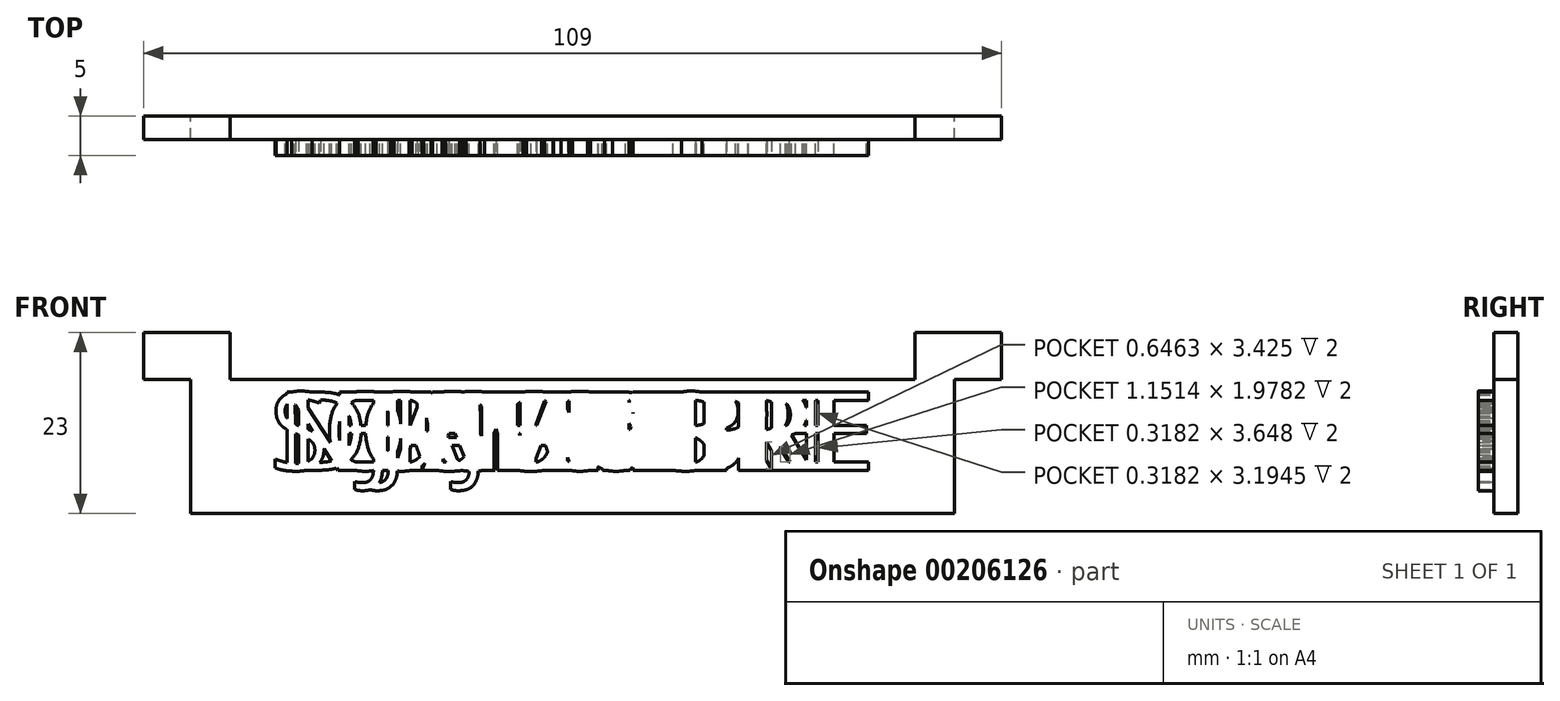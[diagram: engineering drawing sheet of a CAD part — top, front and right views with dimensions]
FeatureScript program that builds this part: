
annotation { "Feature Type Name" : "Feature", "Feature Type Description" : "" }
export const myFeature = defineFeature(function(context is Context, id is Id, definition is map)
    precondition{}
    {
        {
            var Q0;
            Q0=qCreatedBy(makeId("Front.planeOp"),FACE);
            var sketch = newSketch(context, id + "F0", { "sketchPlane" : qUnion([Q0])});
            skLineSegment(sketch, "E0.bottom", {"start": v(-51.5, 23) * mm, "end": v(-40.5, 23) * mm});
            skLineSegment(sketch, "E0.top", {"start": v(-45.5, 0) * mm, "end": v(51.5, 0) * mm});
            skLineSegment(sketch, "E0.left", {"start": v(-51.5, 23) * mm, "end": v(-51.5, 17) * mm});
            skLineSegment(sketch, "E0.right", {"start": v(57.5, 23) * mm, "end": v(57.5, 17) * mm});
            skLineSegment(sketch, "E1.top", {"start": v(-51.5, 17) * mm, "end": v(-45.5, 17) * mm});
            skLineSegment(sketch, "E1.right", {"start": v(-45.5, 0) * mm, "end": v(-45.5, 17) * mm});
            skLineSegment(sketch, "E2.bottom", {"start": v(-51.5, 23) * mm, "end": v(-40.5, 23) * mm, "construction": true});
            skLineSegment(sketch, "E2.top", {"start": v(-51.5, 17) * mm, "end": v(-40.5, 17) * mm, "construction": true});
            skLineSegment(sketch, "E2.left", {"start": v(-51.5, 23) * mm, "end": v(-51.5, 17) * mm, "construction": true});
            skLineSegment(sketch, "E2.right", {"start": v(-40.5, 23) * mm, "end": v(-40.5, 17) * mm, "construction": true});
            skLineSegment(sketch, "E3.top", {"start": v(-40.5, 17) * mm, "end": v(46.5, 17) * mm});
            skLineSegment(sketch, "E3.left", {"start": v(-40.5, 23) * mm, "end": v(-40.5, 17) * mm});
            skLineSegment(sketch, "E3.right", {"start": v(46.5, 23) * mm, "end": v(46.5, 17) * mm});
            skLineSegment(sketch, "E4.top", {"start": v(57.5, 17) * mm, "end": v(51.5, 17) * mm});
            skLineSegment(sketch, "E4.right", {"start": v(51.5, 0) * mm, "end": v(51.5, 17) * mm});
            skLineSegment(sketch, "E5.trimOffspring", {"start": v(46.5, 23) * mm, "end": v(57.5, 23) * mm});
            skSolve(sketch);
        }
        {
            var Q0;
            Q0=makeQuery(id+"F0.imprint","IMPRINT",FACE,{"disambiguationData":[TD([[makeQuery(id+"F0.imprint","IMPRINT",EDGE,{"derivedFrom":sQuery(id+"F0.wireOp",EDGE,"E0.bottom")}),-1.0]])]});
            extrude(context, id + "F1", {"entities" : qUnion([Q0]), "depth" : 3 * mm});
        }
        {
            var Q0;
            Q0=makeQuery(id+"F1.opExtrude","CAP_FACE",FACE,{"disambiguationData":[OSD([sQuery(id+"F0.wireOp",EDGE,"E0.bottom"),sQuery(id+"F0.wireOp",EDGE,"E0.top"),sQuery(id+"F0.wireOp",EDGE,"E0.left"),sQuery(id+"F0.wireOp",EDGE,"E0.right"),sQuery(id+"F0.wireOp",EDGE,"E1.top"),sQuery(id+"F0.wireOp",EDGE,"E1.right"),sQuery(id+"F0.wireOp",EDGE,"E3.top"),sQuery(id+"F0.wireOp",EDGE,"E3.left"),sQuery(id+"F0.wireOp",EDGE,"E3.right"),sQuery(id+"F0.wireOp",EDGE,"E4.top"),sQuery(id+"F0.wireOp",EDGE,"E4.right"),sQuery(id+"F0.wireOp",EDGE,"E5.trimOffspring")])],"isStart":false});
            var sketch = newSketch(context, id + "F2", { "sketchPlane" : qUnion([Q0])});
            skLineSegment(sketch, "E6.0", {"start": v(-45.5, 3.5) * mm, "end": v(-42, 3.5) * mm, "construction": true});
            skLineSegment(sketch, "E7.0", {"start": v(-42, 15.5) * mm, "end": v(48, 15.5) * mm, "construction": true});
            skLineSegment(sketch, "E8.0", {"start": v(-42, 0) * mm, "end": v(-42, 15.5) * mm, "construction": true});
            skText(sketch, "E9", { "text": "JANVIER", "fontName": "OpenSans-Regular.ttf"});
            skLineSegment(sketch, "E10.top", {"start": v(-45.5, 0) * mm, "end": v(-42, 0) * mm, "construction": true});
            skLineSegment(sketch, "E10.left", {"start": v(-45.5, 3.5) * mm, "end": v(-45.5, 0) * mm, "construction": true});
            skLineSegment(sketch, "E10.right", {"start": v(-42, 3.5) * mm, "end": v(-42, 0) * mm, "construction": true});
            skLineSegment(sketch, "E11.0", {"start": v(48, 0) * mm, "end": v(48, 17) * mm, "construction": true});
            skPoint(sketch, "E12.orphan", {"position": v(48, 15.5) * mm});
            skPoint(sketch, "E13.end.orphan", {"position": v(3, 0) * mm});
            skLineSegment(sketch, "E14", {"start": v(3, 17) * mm, "end": v(3, 0) * mm, "construction": true});
            const initialGuessF2  = {"E9": [-0.02358, 0.0055, 1, 0, 0.01]};
            skSetInitialGuess(sketch, initialGuessF2);
            skSolve(sketch);
        }
        {
            var Q0;
            Q0=makeQuery(id+"F2.imprint","IMPRINT",FACE,{"disambiguationData":[TD([[makeQuery(id+"F2.imprint","IMPRINT",EDGE,{"derivedFrom":sQuery(id+"F2.wireOp",EDGE,"E9.sketch_text.stroke-0")}),-1.0]])]});
            var Q1;
            Q1=makeQuery(id+"F2.imprint","IMPRINT",FACE,{"disambiguationData":[TD([[makeQuery(id+"F2.imprint","IMPRINT",EDGE,{"derivedFrom":sQuery(id+"F2.wireOp",EDGE,"E9.sketch_text.stroke-10")}),-1.0]])]});
            var Q2;
            Q2=makeQuery(id+"F2.imprint","IMPRINT",FACE,{"disambiguationData":[TD([[makeQuery(id+"F2.imprint","IMPRINT",EDGE,{"derivedFrom":sQuery(id+"F2.wireOp",EDGE,"E9.sketch_text.stroke-23")}),-1.0]])]});
            var Q3;
            Q3=makeQuery(id+"F2.imprint","IMPRINT",FACE,{"disambiguationData":[TD([[makeQuery(id+"F2.imprint","IMPRINT",EDGE,{"derivedFrom":sQuery(id+"F2.wireOp",EDGE,"E9.sketch_text.stroke-38")}),-1.0]])]});
            var Q4;
            Q4=makeQuery(id+"F2.imprint","IMPRINT",FACE,{"disambiguationData":[TD([[makeQuery(id+"F2.imprint","IMPRINT",EDGE,{"derivedFrom":sQuery(id+"F2.wireOp",EDGE,"E9.sketch_text.stroke-52")}),-1.0]])]});
            var Q5;
            Q5=makeQuery(id+"F2.imprint","IMPRINT",FACE,{"disambiguationData":[TD([[makeQuery(id+"F2.imprint","IMPRINT",EDGE,{"derivedFrom":sQuery(id+"F2.wireOp",EDGE,"E9.sketch_text.stroke-65")}),-1.0]])]});
            var Q6;
            Q6=makeQuery(id+"F2.imprint","IMPRINT",FACE,{"disambiguationData":[TD([[makeQuery(id+"F2.imprint","IMPRINT",EDGE,{"derivedFrom":sQuery(id+"F2.wireOp",EDGE,"E9.sketch_text.stroke-47")}),-1.0]])]});
            extrude(context, id + "F3", {"entities" : qUnion([Q0, Q1, Q2, Q3, Q4, Q5, Q6]), "operationType" : NewBodyOperationType.ADD, "depth" : 2 * mm});
        }
        {
            var Q0;
            Q0=qSketchRegion(id+"F0",true);
            extrude(context, id + "F4", {"entities" : qUnion([Q0]), "depth" : 3 * mm});
        }
        {
            var Q0;
            Q0=makeQuery(id+"F4.opExtrude","CAP_FACE",FACE,{"disambiguationData":[OSD([sQuery(id+"F0.wireOp",EDGE,"E0.bottom"),sQuery(id+"F0.wireOp",EDGE,"E0.top"),sQuery(id+"F0.wireOp",EDGE,"E0.left"),sQuery(id+"F0.wireOp",EDGE,"E0.right"),sQuery(id+"F0.wireOp",EDGE,"E1.top"),sQuery(id+"F0.wireOp",EDGE,"E1.right"),sQuery(id+"F0.wireOp",EDGE,"E3.top"),sQuery(id+"F0.wireOp",EDGE,"E3.left"),sQuery(id+"F0.wireOp",EDGE,"E3.right"),sQuery(id+"F0.wireOp",EDGE,"E4.top"),sQuery(id+"F0.wireOp",EDGE,"E4.right"),sQuery(id+"F0.wireOp",EDGE,"E5.trimOffspring")])],"isStart":false});
            var sketch = newSketch(context, id + "F5", { "sketchPlane" : qUnion([Q0])});
            skText(sketch, "E15", { "text": "FEVRIER", "fontName": "OpenSans-Regular.ttf"});
            skPoint(sketch, "E16.orphan", {"position": v(40.68, 15.5) * mm});
            skPoint(sketch, "E17.end.orphan", {"position": v(-0.5, 0) * mm});
            skPoint(sketch, "E18.orphan", {"position": v(-34.68, 15.5) * mm});
            skLineSegment(sketch, "E19.0", {"start": v(-43.5, 15.5) * mm, "end": v(49.5, 15.5) * mm, "construction": true});
            skPoint(sketch, "E20.start.orphan", {"position": v(3, 17) * mm});
            const initialGuessF5  = {"E15": [-0.0233, 0.0055, 1, 0, 0.01]};
            skSetInitialGuess(sketch, initialGuessF5);
            skSolve(sketch);
        }
        {
            var Q0;
            Q0=makeQuery(id+"F5.imprint","IMPRINT",FACE,{"disambiguationData":[TD([[makeQuery(id+"F5.imprint","IMPRINT",EDGE,{"derivedFrom":sQuery(id+"F5.wireOp",EDGE,"E15.sketch_text.stroke-0")}),-1.0]])]});
            var Q1;
            Q1=makeQuery(id+"F5.imprint","IMPRINT",FACE,{"disambiguationData":[TD([[makeQuery(id+"F5.imprint","IMPRINT",EDGE,{"derivedFrom":sQuery(id+"F5.wireOp",EDGE,"E15.sketch_text.stroke-10")}),-1.0]])]});
            var Q2;
            Q2=makeQuery(id+"F5.imprint","IMPRINT",FACE,{"disambiguationData":[TD([[makeQuery(id+"F5.imprint","IMPRINT",EDGE,{"derivedFrom":sQuery(id+"F5.wireOp",EDGE,"E15.sketch_text.stroke-22")}),-1.0]])]});
            var Q3;
            Q3=makeQuery(id+"F5.imprint","IMPRINT",FACE,{"disambiguationData":[TD([[makeQuery(id+"F5.imprint","IMPRINT",EDGE,{"derivedFrom":sQuery(id+"F5.wireOp",EDGE,"E15.sketch_text.stroke-47")}),-1.0]])]});
            var Q4;
            Q4=makeQuery(id+"F5.imprint","IMPRINT",FACE,{"disambiguationData":[TD([[makeQuery(id+"F5.imprint","IMPRINT",EDGE,{"derivedFrom":sQuery(id+"F5.wireOp",EDGE,"E15.sketch_text.stroke-65")}),-1.0]])]});
            var Q5;
            Q5=makeQuery(id+"F5.imprint","IMPRINT",FACE,{"disambiguationData":[TD([[makeQuery(id+"F5.imprint","IMPRINT",EDGE,{"derivedFrom":sQuery(id+"F5.wireOp",EDGE,"E15.sketch_text.stroke-79")}),-1.0]])]});
            var Q6;
            Q6=makeQuery(id+"F2.imprint","IMPRINT",FACE,{"disambiguationData":[TD([[makeQuery(id+"F2.imprint","IMPRINT",EDGE,{"derivedFrom":sQuery(id+"F2.wireOp",EDGE,"E9.sketch_text.stroke-51")}),-1.0]])]});
            var Q7;
            Q7=makeQuery(id+"F2.imprint","IMPRINT",FACE,{"disambiguationData":[TD([[makeQuery(id+"F2.imprint","IMPRINT",EDGE,{"derivedFrom":sQuery(id+"F2.wireOp",EDGE,"E9.sketch_text.stroke-47")}),-1.0]])]});
            extrude(context, id + "F6", {"entities" : qUnion([Q0, Q1, Q2, Q3, Q4, Q5, Q6, Q7]), "operationType" : NewBodyOperationType.ADD, "depth" : 2 * mm});
        }
        {
            var Q0;
            Q0=makeQuery(id+"F0.imprint","IMPRINT",FACE,{"disambiguationData":[TD([[makeQuery(id+"F0.imprint","IMPRINT",EDGE,{"derivedFrom":sQuery(id+"F0.wireOp",EDGE,"E0.bottom")}),-1.0]])]});
            extrude(context, id + "F7", {"entities" : qUnion([Q0]), "depth" : 3 * mm});
        }
        {
            var Q0;
            Q0=makeQuery(id+"F7.opExtrude","CAP_FACE",FACE,{"disambiguationData":[OSD([sQuery(id+"F0.wireOp",EDGE,"E0.bottom"),sQuery(id+"F0.wireOp",EDGE,"E0.top"),sQuery(id+"F0.wireOp",EDGE,"E0.left"),sQuery(id+"F0.wireOp",EDGE,"E0.right"),sQuery(id+"F0.wireOp",EDGE,"E1.top"),sQuery(id+"F0.wireOp",EDGE,"E1.right"),sQuery(id+"F0.wireOp",EDGE,"E3.top"),sQuery(id+"F0.wireOp",EDGE,"E3.left"),sQuery(id+"F0.wireOp",EDGE,"E3.right"),sQuery(id+"F0.wireOp",EDGE,"E4.top"),sQuery(id+"F0.wireOp",EDGE,"E4.right"),sQuery(id+"F0.wireOp",EDGE,"E5.trimOffspring")])],"isStart":false});
            var sketch = newSketch(context, id + "F8", { "sketchPlane" : qUnion([Q0])});
            skText(sketch, "E21", { "text": "MARS", "fontName": "OpenSans-Regular.ttf"});
            skPoint(sketch, "E22.orphan", {"position": v(33.28, 15.5) * mm});
            skPoint(sketch, "E23.end.orphan", {"position": v(0, -12.7) * mm});
            skPoint(sketch, "E24.orphan", {"position": v(-27.28, 15.5) * mm});
            skPoint(sketch, "E25.start.orphan", {"position": v(0, 4.3) * mm});
            skLineSegment(sketch, "E26.0", {"start": v(-43.5, 15.5) * mm, "end": v(49.5, 15.5) * mm, "construction": true});
            const initialGuessF8  = {"E21": [-0.01589, 0.0055, 1, 0, 0.01]};
            skSetInitialGuess(sketch, initialGuessF8);
            skSolve(sketch);
        }
        {
            var Q0;
            Q0=makeQuery(id+"F8.imprint","IMPRINT",FACE,{"disambiguationData":[TD([[makeQuery(id+"F8.imprint","IMPRINT",EDGE,{"derivedFrom":sQuery(id+"F8.wireOp",EDGE,"E21.sketch_text.stroke-0")}),-1.0]])]});
            var Q1;
            Q1=makeQuery(id+"F8.imprint","IMPRINT",FACE,{"disambiguationData":[TD([[makeQuery(id+"F8.imprint","IMPRINT",EDGE,{"derivedFrom":sQuery(id+"F8.wireOp",EDGE,"E21.sketch_text.stroke-18")}),-1.0]])]});
            var Q2;
            Q2=makeQuery(id+"F8.imprint","IMPRINT",FACE,{"disambiguationData":[TD([[makeQuery(id+"F8.imprint","IMPRINT",EDGE,{"derivedFrom":sQuery(id+"F8.wireOp",EDGE,"E21.sketch_text.stroke-31")}),-1.0]])]});
            var Q3;
            Q3=makeQuery(id+"F8.imprint","IMPRINT",FACE,{"disambiguationData":[TD([[makeQuery(id+"F8.imprint","IMPRINT",EDGE,{"derivedFrom":sQuery(id+"F8.wireOp",EDGE,"E21.sketch_text.stroke-49")}),-1.0]])]});
            var Q4;
            Q4=makeQuery(id+"F8.imprint","IMPRINT",FACE,{"disambiguationData":[TD([[makeQuery(id+"F8.imprint","IMPRINT",EDGE,{"derivedFrom":sQuery(id+"F8.wireOp",EDGE,"E21.sketch_text.stroke-64")}),-1.0]])]});
            extrude(context, id + "F9", {"entities" : qUnion([Q0, Q1, Q2, Q3, Q4]), "operationType" : NewBodyOperationType.ADD, "depth" : 2 * mm});
        }
        {
            var Q0;
            Q0=makeQuery(id+"F0.imprint","IMPRINT",FACE,{"disambiguationData":[TD([[makeQuery(id+"F0.imprint","IMPRINT",EDGE,{"derivedFrom":sQuery(id+"F0.wireOp",EDGE,"E0.bottom")}),-1.0]])]});
            extrude(context, id + "F10", {"entities" : qUnion([Q0]), "depth" : 3 * mm});
        }
        {
            var Q0;
            Q0=makeQuery(id+"F10.opExtrude","CAP_FACE",FACE,{"disambiguationData":[OSD([sQuery(id+"F0.wireOp",EDGE,"E0.bottom"),sQuery(id+"F0.wireOp",EDGE,"E0.top"),sQuery(id+"F0.wireOp",EDGE,"E0.left"),sQuery(id+"F0.wireOp",EDGE,"E0.right"),sQuery(id+"F0.wireOp",EDGE,"E1.top"),sQuery(id+"F0.wireOp",EDGE,"E1.right"),sQuery(id+"F0.wireOp",EDGE,"E3.top"),sQuery(id+"F0.wireOp",EDGE,"E3.left"),sQuery(id+"F0.wireOp",EDGE,"E3.right"),sQuery(id+"F0.wireOp",EDGE,"E4.top"),sQuery(id+"F0.wireOp",EDGE,"E4.right"),sQuery(id+"F0.wireOp",EDGE,"E5.trimOffspring")])],"isStart":false});
            var sketch = newSketch(context, id + "F11", { "sketchPlane" : qUnion([Q0])});
            skText(sketch, "E27", { "text": "AVRIL", "fontName": "OpenSans-Regular.ttf"});
            skPoint(sketch, "E28.orphan", {"position": v(33.04, 15.5) * mm});
            skPoint(sketch, "E29.end.orphan", {"position": v(0.3, -20.32) * mm});
            skPoint(sketch, "E30.orphan", {"position": v(-27.04, 15.5) * mm});
            skPoint(sketch, "E31.start.orphan", {"position": v(0.3, -3.32) * mm});
            skLineSegment(sketch, "E32.0", {"start": v(-43.5, 15.5) * mm, "end": v(49.5, 15.5) * mm});
            const initialGuessF11  = {"E27": [-0.01565, 0.0055, 1, 0, 0.01]};
            skSetInitialGuess(sketch, initialGuessF11);
            skSolve(sketch);
        }
        {
            var Q0;
            Q0=makeQuery(id+"F11.imprint","IMPRINT",FACE,{"disambiguationData":[TD([[makeQuery(id+"F11.imprint","IMPRINT",EDGE,{"derivedFrom":sQuery(id+"F11.wireOp",EDGE,"E27.sketch_text.stroke-0")}),-1.0]])]});
            var Q1;
            Q1=makeQuery(id+"F11.imprint","IMPRINT",FACE,{"disambiguationData":[TD([[makeQuery(id+"F11.imprint","IMPRINT",EDGE,{"derivedFrom":sQuery(id+"F11.wireOp",EDGE,"E27.sketch_text.stroke-13")}),-1.0]])]});
            var Q2;
            Q2=makeQuery(id+"F11.imprint","IMPRINT",FACE,{"disambiguationData":[TD([[makeQuery(id+"F11.imprint","IMPRINT",EDGE,{"derivedFrom":sQuery(id+"F11.wireOp",EDGE,"E27.sketch_text.stroke-28")}),-1.0]])]});
            var Q3;
            Q3=makeQuery(id+"F11.imprint","IMPRINT",FACE,{"disambiguationData":[TD([[makeQuery(id+"F11.imprint","IMPRINT",EDGE,{"derivedFrom":sQuery(id+"F11.wireOp",EDGE,"E27.sketch_text.stroke-46")}),-1.0]])]});
            var Q4;
            Q4=makeQuery(id+"F11.imprint","IMPRINT",FACE,{"disambiguationData":[TD([[makeQuery(id+"F11.imprint","IMPRINT",EDGE,{"derivedFrom":sQuery(id+"F11.wireOp",EDGE,"E27.sketch_text.stroke-40")}),-1.0]])]});
            extrude(context, id + "F12", {"entities" : qUnion([Q0, Q1, Q2, Q3, Q4]), "operationType" : NewBodyOperationType.ADD, "depth" : 2 * mm});
        }
        {
            var Q0;
            Q0=makeQuery(id+"F0.imprint","IMPRINT",FACE,{"disambiguationData":[TD([[makeQuery(id+"F0.imprint","IMPRINT",EDGE,{"derivedFrom":sQuery(id+"F0.wireOp",EDGE,"E0.bottom")}),-1.0]])]});
            extrude(context, id + "F13", {"entities" : qUnion([Q0]), "depth" : 3 * mm});
        }
        {
            var Q0;
            Q0=makeQuery(id+"F13.opExtrude","CAP_FACE",FACE,{"disambiguationData":[OSD([sQuery(id+"F0.wireOp",EDGE,"E0.bottom"),sQuery(id+"F0.wireOp",EDGE,"E0.top"),sQuery(id+"F0.wireOp",EDGE,"E0.left"),sQuery(id+"F0.wireOp",EDGE,"E0.right"),sQuery(id+"F0.wireOp",EDGE,"E1.top"),sQuery(id+"F0.wireOp",EDGE,"E1.right"),sQuery(id+"F0.wireOp",EDGE,"E3.top"),sQuery(id+"F0.wireOp",EDGE,"E3.left"),sQuery(id+"F0.wireOp",EDGE,"E3.right"),sQuery(id+"F0.wireOp",EDGE,"E4.top"),sQuery(id+"F0.wireOp",EDGE,"E4.right"),sQuery(id+"F0.wireOp",EDGE,"E5.trimOffspring")])],"isStart":false});
            var sketch = newSketch(context, id + "F14", { "sketchPlane" : qUnion([Q0])});
            skText(sketch, "E33", { "text": "MAI", "fontName": "OpenSans-Regular.ttf"});
            skPoint(sketch, "E34.orphan", {"position": v(26.76, 15.5) * mm});
            skPoint(sketch, "E35.end.orphan", {"position": v(0.48, -24.9) * mm});
            skPoint(sketch, "E36.orphan", {"position": v(-20.76, 15.5) * mm});
            skPoint(sketch, "E37.start.orphan", {"position": v(0.48, -7.9) * mm});
            skLineSegment(sketch, "E38.0", {"start": v(-33.67, 15.5) * mm, "end": v(39.67, 15.5) * mm});
            skLineSegment(sketch, "E39.0", {"start": v(-43.5, 15.5) * mm, "end": v(49.5, 15.5) * mm});
            const initialGuessF14  = {"E33": [-0.00937, 0.0055, 1, 0, 0.01]};
            skSetInitialGuess(sketch, initialGuessF14);
            skSolve(sketch);
        }
        {
            var Q0;
            Q0=makeQuery(id+"F0.imprint","IMPRINT",FACE,{"disambiguationData":[TD([[makeQuery(id+"F0.imprint","IMPRINT",EDGE,{"derivedFrom":sQuery(id+"F0.wireOp",EDGE,"E0.bottom")}),-1.0]])]});
            extrude(context, id + "F15", {"entities" : qUnion([Q0]), "depth" : 3 * mm});
        }
        {
            var Q0;
            Q0=makeQuery(id+"F15.opExtrude","CAP_FACE",FACE,{"disambiguationData":[OSD([sQuery(id+"F0.wireOp",EDGE,"E0.bottom"),sQuery(id+"F0.wireOp",EDGE,"E0.top"),sQuery(id+"F0.wireOp",EDGE,"E0.left"),sQuery(id+"F0.wireOp",EDGE,"E0.right"),sQuery(id+"F0.wireOp",EDGE,"E1.top"),sQuery(id+"F0.wireOp",EDGE,"E1.right"),sQuery(id+"F0.wireOp",EDGE,"E3.top"),sQuery(id+"F0.wireOp",EDGE,"E3.left"),sQuery(id+"F0.wireOp",EDGE,"E3.right"),sQuery(id+"F0.wireOp",EDGE,"E4.top"),sQuery(id+"F0.wireOp",EDGE,"E4.right"),sQuery(id+"F0.wireOp",EDGE,"E5.trimOffspring")])],"isStart":false});
            var sketch = newSketch(context, id + "F16", { "sketchPlane" : qUnion([Q0])});
            skText(sketch, "E40", { "text": "JUIN", "fontName": "OpenSans-Regular.ttf"});
            skPoint(sketch, "E41.orphan", {"position": v(28.78, 15.5) * mm});
            skPoint(sketch, "E42.end.orphan", {"position": v(0.65, -29.76) * mm});
            skPoint(sketch, "E43.orphan", {"position": v(-22.78, 15.5) * mm});
            skPoint(sketch, "E44.start.orphan", {"position": v(0.65, -12.76) * mm});
            skLineSegment(sketch, "E45.0", {"start": v(-35.7, 15.5) * mm, "end": v(41.7, 15.5) * mm});
            skLineSegment(sketch, "E46.0", {"start": v(-39.39, 15.5) * mm, "end": v(45.39, 15.5) * mm});
            skLineSegment(sketch, "E47.0", {"start": v(-43.5, 15.5) * mm, "end": v(49.5, 15.5) * mm});
            const initialGuessF16  = {"E40": [-0.0114, 0.0055, 1, 0, 0.01]};
            skSetInitialGuess(sketch, initialGuessF16);
            skSolve(sketch);
        }
        {
            var Q0;
            Q0=makeQuery(id+"F0.imprint","IMPRINT",FACE,{"disambiguationData":[TD([[makeQuery(id+"F0.imprint","IMPRINT",EDGE,{"derivedFrom":sQuery(id+"F0.wireOp",EDGE,"E0.bottom")}),-1.0]])]});
            extrude(context, id + "F17", {"entities" : qUnion([Q0]), "depth" : 3 * mm});
        }
        {
            var Q0;
            Q0=makeQuery(id+"F17.opExtrude","CAP_FACE",FACE,{"disambiguationData":[OSD([sQuery(id+"F0.wireOp",EDGE,"E0.bottom"),sQuery(id+"F0.wireOp",EDGE,"E0.top"),sQuery(id+"F0.wireOp",EDGE,"E0.left"),sQuery(id+"F0.wireOp",EDGE,"E0.right"),sQuery(id+"F0.wireOp",EDGE,"E1.top"),sQuery(id+"F0.wireOp",EDGE,"E1.right"),sQuery(id+"F0.wireOp",EDGE,"E3.top"),sQuery(id+"F0.wireOp",EDGE,"E3.left"),sQuery(id+"F0.wireOp",EDGE,"E3.right"),sQuery(id+"F0.wireOp",EDGE,"E4.top"),sQuery(id+"F0.wireOp",EDGE,"E4.right"),sQuery(id+"F0.wireOp",EDGE,"E5.trimOffspring")])],"isStart":false});
            var sketch = newSketch(context, id + "F18", { "sketchPlane" : qUnion([Q0])});
            skText(sketch, "E48", { "text": "JULLIET", "fontName": "OpenSans-Regular.ttf"});
            skPoint(sketch, "E49.orphan", {"position": v(39.08, 15.5) * mm});
            skPoint(sketch, "E50.end.orphan", {"position": v(0.82, -34.76) * mm});
            skPoint(sketch, "E51.orphan", {"position": v(-33.08, 15.5) * mm});
            skPoint(sketch, "E52.start.orphan", {"position": v(0.82, -17.76) * mm});
            skLineSegment(sketch, "E53.0", {"start": v(-45.99, 15.5) * mm, "end": v(51.99, 15.5) * mm});
            skLineSegment(sketch, "E54.0", {"start": v(-49.68, 15.5) * mm, "end": v(55.68, 15.5) * mm});
            skLineSegment(sketch, "E55.0", {"start": v(-48.1, 15.5) * mm, "end": v(54.1, 15.5) * mm});
            skLineSegment(sketch, "E56.0", {"start": v(-43.5, 15.5) * mm, "end": v(49.5, 15.5) * mm});
            const initialGuessF18  = {"E48": [-0.02169, 0.0055, 1, 0, 0.01]};
            skSetInitialGuess(sketch, initialGuessF18);
            skSolve(sketch);
        }
        {
            var Q0;
            Q0=makeQuery(id+"F0.imprint","IMPRINT",FACE,{"disambiguationData":[TD([[makeQuery(id+"F0.imprint","IMPRINT",EDGE,{"derivedFrom":sQuery(id+"F0.wireOp",EDGE,"E0.bottom")}),-1.0]])]});
            extrude(context, id + "F19", {"entities" : qUnion([Q0]), "depth" : 3 * mm});
        }
        {
            var Q0;
            Q0=makeQuery(id+"F19.opExtrude","CAP_FACE",FACE,{"disambiguationData":[OSD([sQuery(id+"F0.wireOp",EDGE,"E0.bottom"),sQuery(id+"F0.wireOp",EDGE,"E0.top"),sQuery(id+"F0.wireOp",EDGE,"E0.left"),sQuery(id+"F0.wireOp",EDGE,"E0.right"),sQuery(id+"F0.wireOp",EDGE,"E1.top"),sQuery(id+"F0.wireOp",EDGE,"E1.right"),sQuery(id+"F0.wireOp",EDGE,"E3.top"),sQuery(id+"F0.wireOp",EDGE,"E3.left"),sQuery(id+"F0.wireOp",EDGE,"E3.right"),sQuery(id+"F0.wireOp",EDGE,"E4.top"),sQuery(id+"F0.wireOp",EDGE,"E4.right"),sQuery(id+"F0.wireOp",EDGE,"E5.trimOffspring")])],"isStart":false});
            var sketch = newSketch(context, id + "F20", { "sketchPlane" : qUnion([Q0])});
            skText(sketch, "E57", { "text": "AOUT", "fontName": "OpenSans-Regular.ttf"});
            skPoint(sketch, "E58.orphan", {"position": v(33.48, 15.5) * mm});
            skPoint(sketch, "E59.end.orphan", {"position": v(1, -39.82) * mm});
            skPoint(sketch, "E60.orphan", {"position": v(-27.48, 15.5) * mm});
            skPoint(sketch, "E61.start.orphan", {"position": v(1, -22.82) * mm});
            skLineSegment(sketch, "E62.0", {"start": v(-40.39, 15.5) * mm, "end": v(46.39, 15.5) * mm});
            skLineSegment(sketch, "E63.0", {"start": v(-44.08, 15.5) * mm, "end": v(50.08, 15.5) * mm});
            skLineSegment(sketch, "E64.0", {"start": v(-42.5, 15.5) * mm, "end": v(48.5, 15.5) * mm});
            skLineSegment(sketch, "E65.0", {"start": v(-43.69, 15.5) * mm, "end": v(49.69, 15.5) * mm});
            skLineSegment(sketch, "E66.0", {"start": v(-43.5, 15.5) * mm, "end": v(49.5, 15.5) * mm});
            const initialGuessF20  = {"E57": [-0.01609, 0.0055, 1, 0, 0.01]};
            skSetInitialGuess(sketch, initialGuessF20);
            skSolve(sketch);
        }
        {
            var Q0;
            Q0=makeQuery(id+"F0.imprint","IMPRINT",FACE,{"disambiguationData":[TD([[makeQuery(id+"F0.imprint","IMPRINT",EDGE,{"derivedFrom":sQuery(id+"F0.wireOp",EDGE,"E0.bottom")}),-1.0]])]});
            extrude(context, id + "F21", {"entities" : qUnion([Q0]), "depth" : 3 * mm});
        }
        {
            var Q0;
            Q0=makeQuery(id+"F21.opExtrude","CAP_FACE",FACE,{"disambiguationData":[OSD([sQuery(id+"F0.wireOp",EDGE,"E0.bottom"),sQuery(id+"F0.wireOp",EDGE,"E0.top"),sQuery(id+"F0.wireOp",EDGE,"E0.left"),sQuery(id+"F0.wireOp",EDGE,"E0.right"),sQuery(id+"F0.wireOp",EDGE,"E1.top"),sQuery(id+"F0.wireOp",EDGE,"E1.right"),sQuery(id+"F0.wireOp",EDGE,"E3.top"),sQuery(id+"F0.wireOp",EDGE,"E3.left"),sQuery(id+"F0.wireOp",EDGE,"E3.right"),sQuery(id+"F0.wireOp",EDGE,"E4.top"),sQuery(id+"F0.wireOp",EDGE,"E4.right"),sQuery(id+"F0.wireOp",EDGE,"E5.trimOffspring")])],"isStart":false});
            var sketch = newSketch(context, id + "F22", { "sketchPlane" : qUnion([Q0])});
            skText(sketch, "E67", { "text": "SEPTEMBRE", "fontName": "OpenSans-Regular.ttf"});
            skPoint(sketch, "E68.orphan", {"position": v(52.9, 15.5) * mm});
            skPoint(sketch, "E69.end.orphan", {"position": v(1.16, -44.91) * mm});
            skPoint(sketch, "E70.orphan", {"position": v(-46.9, 15.5) * mm});
            skPoint(sketch, "E71.start.orphan", {"position": v(1.16, -27.91) * mm});
            const initialGuessF22  = {"E67": [-0.03552, 0.0055, 1, 0, 0.01]};
            skSetInitialGuess(sketch, initialGuessF22);
            skSolve(sketch);
        }
        {
            var Q0;
            Q0=makeQuery(id+"F0.imprint","IMPRINT",FACE,{"disambiguationData":[TD([[makeQuery(id+"F0.imprint","IMPRINT",EDGE,{"derivedFrom":sQuery(id+"F0.wireOp",EDGE,"E0.bottom")}),-1.0]])]});
            extrude(context, id + "F23", {"entities" : qUnion([Q0]), "depth" : 3 * mm});
        }
        {
            var Q0;
            Q0=makeQuery(id+"F23.opExtrude","CAP_FACE",FACE,{"disambiguationData":[OSD([sQuery(id+"F0.wireOp",EDGE,"E0.bottom"),sQuery(id+"F0.wireOp",EDGE,"E0.top"),sQuery(id+"F0.wireOp",EDGE,"E0.left"),sQuery(id+"F0.wireOp",EDGE,"E0.right"),sQuery(id+"F0.wireOp",EDGE,"E1.top"),sQuery(id+"F0.wireOp",EDGE,"E1.right"),sQuery(id+"F0.wireOp",EDGE,"E3.top"),sQuery(id+"F0.wireOp",EDGE,"E3.left"),sQuery(id+"F0.wireOp",EDGE,"E3.right"),sQuery(id+"F0.wireOp",EDGE,"E4.top"),sQuery(id+"F0.wireOp",EDGE,"E4.right"),sQuery(id+"F0.wireOp",EDGE,"E5.trimOffspring")])],"isStart":false});
            var sketch = newSketch(context, id + "F24", { "sketchPlane" : qUnion([Q0])});
            skText(sketch, "E72", { "text": "OCTOBRE", "fontName": "OpenSans-Regular.ttf"});
            skPoint(sketch, "E73.orphan", {"position": v(46.12, 15.5) * mm});
            skPoint(sketch, "E74.end.orphan", {"position": v(1.08, -34.46) * mm});
            skPoint(sketch, "E75.orphan", {"position": v(-40.12, 15.5) * mm});
            skPoint(sketch, "E76.start.orphan", {"position": v(1.08, -17.46) * mm});
            skLineSegment(sketch, "E77.0", {"start": v(-42.5, 15.5) * mm, "end": v(48.5, 15.5) * mm});
            const initialGuessF24  = {"E72": [-0.02873, 0.0055, 1, 0, 0.01]};
            skSetInitialGuess(sketch, initialGuessF24);
            skSolve(sketch);
        }
        {
            var Q0;
            Q0=makeQuery(id+"F0.imprint","IMPRINT",FACE,{"disambiguationData":[TD([[makeQuery(id+"F0.imprint","IMPRINT",EDGE,{"derivedFrom":sQuery(id+"F0.wireOp",EDGE,"E0.bottom")}),-1.0]])]});
            extrude(context, id + "F25", {"entities" : qUnion([Q0]), "depth" : 3 * mm});
        }
        {
            var Q0;
            Q0=makeQuery(id+"F25.opExtrude","CAP_FACE",FACE,{"disambiguationData":[OSD([sQuery(id+"F0.wireOp",EDGE,"E0.bottom"),sQuery(id+"F0.wireOp",EDGE,"E0.top"),sQuery(id+"F0.wireOp",EDGE,"E0.left"),sQuery(id+"F0.wireOp",EDGE,"E0.right"),sQuery(id+"F0.wireOp",EDGE,"E1.top"),sQuery(id+"F0.wireOp",EDGE,"E1.right"),sQuery(id+"F0.wireOp",EDGE,"E3.top"),sQuery(id+"F0.wireOp",EDGE,"E3.left"),sQuery(id+"F0.wireOp",EDGE,"E3.right"),sQuery(id+"F0.wireOp",EDGE,"E4.top"),sQuery(id+"F0.wireOp",EDGE,"E4.right"),sQuery(id+"F0.wireOp",EDGE,"E5.trimOffspring")])],"isStart":false});
            var sketch = newSketch(context, id + "F26", { "sketchPlane" : qUnion([Q0])});
            skText(sketch, "E78", { "text": "NOVEMBRE", "fontName": "OpenSans-Regular.ttf"});
            skPoint(sketch, "E79.orphan", {"position": v(51.99, 15.5) * mm});
            skPoint(sketch, "E80.end.orphan", {"position": v(1.08, -34.46) * mm});
            skPoint(sketch, "E81.orphan", {"position": v(-45.99, 15.5) * mm});
            skPoint(sketch, "E82.start.orphan", {"position": v(1.08, -17.46) * mm});
            skLineSegment(sketch, "E83.0", {"start": v(-42.5, 15.5) * mm, "end": v(48.5, 15.5) * mm});
            const initialGuessF26  = {"E78": [-0.0346, 0.0055, 1, 0, 0.01]};
            skSetInitialGuess(sketch, initialGuessF26);
            skSolve(sketch);
        }
        {
            var Q0;
            Q0=makeQuery(id+"F0.imprint","IMPRINT",FACE,{"disambiguationData":[TD([[makeQuery(id+"F0.imprint","IMPRINT",EDGE,{"derivedFrom":sQuery(id+"F0.wireOp",EDGE,"E0.bottom")}),-1.0]])]});
            extrude(context, id + "F27", {"entities" : qUnion([Q0]), "depth" : 3 * mm});
        }
        {
            var Q0;
            Q0=makeQuery(id+"F27.opExtrude","CAP_FACE",FACE,{"disambiguationData":[OSD([sQuery(id+"F0.wireOp",EDGE,"E0.bottom"),sQuery(id+"F0.wireOp",EDGE,"E0.top"),sQuery(id+"F0.wireOp",EDGE,"E0.left"),sQuery(id+"F0.wireOp",EDGE,"E0.right"),sQuery(id+"F0.wireOp",EDGE,"E1.top"),sQuery(id+"F0.wireOp",EDGE,"E1.right"),sQuery(id+"F0.wireOp",EDGE,"E3.top"),sQuery(id+"F0.wireOp",EDGE,"E3.left"),sQuery(id+"F0.wireOp",EDGE,"E3.right"),sQuery(id+"F0.wireOp",EDGE,"E4.top"),sQuery(id+"F0.wireOp",EDGE,"E4.right"),sQuery(id+"F0.wireOp",EDGE,"E5.trimOffspring")])],"isStart":false});
            var sketch = newSketch(context, id + "F28", { "sketchPlane" : qUnion([Q0])});
            skText(sketch, "E84", { "text": "DECEMBRE", "fontName": "OpenSans-Regular.ttf"});
            skPoint(sketch, "E85.orphan", {"position": v(50.52, 15.5) * mm});
            skPoint(sketch, "E86.end.orphan", {"position": v(1.08, -34.46) * mm});
            skPoint(sketch, "E87.orphan", {"position": v(-44.52, 15.5) * mm});
            skPoint(sketch, "E88.start.orphan", {"position": v(1.08, -17.46) * mm});
            skLineSegment(sketch, "E89.0", {"start": v(-42.5, 15.5) * mm, "end": v(48.5, 15.5) * mm});
            const initialGuessF28  = {"E84": [-0.03313, 0.0055, 1, 0, 0.01]};
            skSetInitialGuess(sketch, initialGuessF28);
            skSolve(sketch);
        }
        {
            var Q0;
            Q0=makeQuery(id+"F28.imprint","IMPRINT",FACE,{"disambiguationData":[TD([[makeQuery(id+"F28.imprint","IMPRINT",EDGE,{"derivedFrom":sQuery(id+"F28.wireOp",EDGE,"E84.sketch_text.stroke-0")}),-1.0]])]});
            var Q1;
            Q1=makeQuery(id+"F28.imprint","IMPRINT",FACE,{"disambiguationData":[TD([[makeQuery(id+"F28.imprint","IMPRINT",EDGE,{"derivedFrom":sQuery(id+"F28.wireOp",EDGE,"E84.sketch_text.stroke-14")}),-1.0]])]});
            var Q2;
            Q2=makeQuery(id+"F28.imprint","IMPRINT",FACE,{"disambiguationData":[TD([[makeQuery(id+"F28.imprint","IMPRINT",EDGE,{"derivedFrom":sQuery(id+"F28.wireOp",EDGE,"E84.sketch_text.stroke-26")}),-1.0]])]});
            var Q3;
            Q3=makeQuery(id+"F28.imprint","IMPRINT",FACE,{"disambiguationData":[TD([[makeQuery(id+"F28.imprint","IMPRINT",EDGE,{"derivedFrom":sQuery(id+"F28.wireOp",EDGE,"E84.sketch_text.stroke-41")}),-1.0]])]});
            var Q4;
            Q4=makeQuery(id+"F28.imprint","IMPRINT",FACE,{"disambiguationData":[TD([[makeQuery(id+"F28.imprint","IMPRINT",EDGE,{"derivedFrom":sQuery(id+"F28.wireOp",EDGE,"E84.sketch_text.stroke-53")}),-1.0]])]});
            var Q5;
            Q5=makeQuery(id+"F28.imprint","IMPRINT",FACE,{"disambiguationData":[TD([[makeQuery(id+"F28.imprint","IMPRINT",EDGE,{"derivedFrom":sQuery(id+"F28.wireOp",EDGE,"E84.sketch_text.stroke-71")}),-1.0]])]});
            var Q6;
            Q6=makeQuery(id+"F28.imprint","IMPRINT",FACE,{"disambiguationData":[TD([[makeQuery(id+"F28.imprint","IMPRINT",EDGE,{"derivedFrom":sQuery(id+"F28.wireOp",EDGE,"E84.sketch_text.stroke-96")}),-1.0]])]});
            var Q7;
            Q7=makeQuery(id+"F28.imprint","IMPRINT",FACE,{"disambiguationData":[TD([[makeQuery(id+"F28.imprint","IMPRINT",EDGE,{"derivedFrom":sQuery(id+"F28.wireOp",EDGE,"E84.sketch_text.stroke-108")}),-1.0]])]});
            var Q8;
            Q8=makeQuery(id+"F28.imprint","IMPRINT",FACE,{"disambiguationData":[TD([[makeQuery(id+"F28.imprint","IMPRINT",EDGE,{"derivedFrom":sQuery(id+"F28.wireOp",EDGE,"E84.sketch_text.stroke-114")}),-1.0]])]});
            extrude(context, id + "F29", {"entities" : qUnion([Q0, Q1, Q2, Q3, Q4, Q5, Q6, Q7, Q8]), "operationType" : NewBodyOperationType.ADD, "depth" : 2 * mm});
        }
        {
            var Q0;
            Q0=makeQuery(id+"F26.imprint","IMPRINT",FACE,{"disambiguationData":[TD([[makeQuery(id+"F26.imprint","IMPRINT",EDGE,{"derivedFrom":sQuery(id+"F26.wireOp",EDGE,"E78.sketch_text.stroke-0")}),-1.0]])]});
            var Q1;
            Q1=makeQuery(id+"F26.imprint","IMPRINT",FACE,{"disambiguationData":[TD([[makeQuery(id+"F26.imprint","IMPRINT",EDGE,{"derivedFrom":sQuery(id+"F26.wireOp",EDGE,"E78.sketch_text.stroke-15")}),-1.0]])]});
            var Q2;
            Q2=makeQuery(id+"F26.imprint","IMPRINT",FACE,{"disambiguationData":[TD([[makeQuery(id+"F26.imprint","IMPRINT",EDGE,{"derivedFrom":sQuery(id+"F26.wireOp",EDGE,"E78.sketch_text.stroke-31")}),-1.0]])]});
            var Q3;
            Q3=makeQuery(id+"F26.imprint","IMPRINT",FACE,{"disambiguationData":[TD([[makeQuery(id+"F26.imprint","IMPRINT",EDGE,{"derivedFrom":sQuery(id+"F26.wireOp",EDGE,"E78.sketch_text.stroke-40")}),-1.0]])]});
            var Q4;
            Q4=makeQuery(id+"F26.imprint","IMPRINT",FACE,{"disambiguationData":[TD([[makeQuery(id+"F26.imprint","IMPRINT",EDGE,{"derivedFrom":sQuery(id+"F26.wireOp",EDGE,"E78.sketch_text.stroke-52")}),-1.0]])]});
            var Q5;
            Q5=makeQuery(id+"F26.imprint","IMPRINT",FACE,{"disambiguationData":[TD([[makeQuery(id+"F26.imprint","IMPRINT",EDGE,{"derivedFrom":sQuery(id+"F26.wireOp",EDGE,"E78.sketch_text.stroke-70")}),-1.0]])]});
            var Q6;
            Q6=makeQuery(id+"F26.imprint","IMPRINT",FACE,{"disambiguationData":[TD([[makeQuery(id+"F26.imprint","IMPRINT",EDGE,{"derivedFrom":sQuery(id+"F26.wireOp",EDGE,"E78.sketch_text.stroke-95")}),-1.0]])]});
            var Q7;
            Q7=makeQuery(id+"F26.imprint","IMPRINT",FACE,{"disambiguationData":[TD([[makeQuery(id+"F26.imprint","IMPRINT",EDGE,{"derivedFrom":sQuery(id+"F26.wireOp",EDGE,"E78.sketch_text.stroke-107")}),-1.0]])]});
            var Q8;
            Q8=makeQuery(id+"F26.imprint","IMPRINT",FACE,{"disambiguationData":[TD([[makeQuery(id+"F26.imprint","IMPRINT",EDGE,{"derivedFrom":sQuery(id+"F26.wireOp",EDGE,"E78.sketch_text.stroke-113")}),-1.0]])]});
            extrude(context, id + "F30", {"entities" : qUnion([Q0, Q1, Q2, Q3, Q4, Q5, Q6, Q7, Q8]), "operationType" : NewBodyOperationType.ADD, "depth" : 2 * mm});
        }
        {
            var Q0;
            Q0=makeQuery(id+"F24.imprint","IMPRINT",FACE,{"disambiguationData":[TD([[makeQuery(id+"F24.imprint","IMPRINT",EDGE,{"derivedFrom":sQuery(id+"F24.wireOp",EDGE,"E72.sketch_text.stroke-0")}),-1.0]])]});
            var Q1;
            Q1=makeQuery(id+"F24.imprint","IMPRINT",FACE,{"disambiguationData":[TD([[makeQuery(id+"F24.imprint","IMPRINT",EDGE,{"derivedFrom":sQuery(id+"F24.wireOp",EDGE,"E72.sketch_text.stroke-16")}),-1.0]])]});
            var Q2;
            Q2=makeQuery(id+"F24.imprint","IMPRINT",FACE,{"disambiguationData":[TD([[makeQuery(id+"F24.imprint","IMPRINT",EDGE,{"derivedFrom":sQuery(id+"F24.wireOp",EDGE,"E72.sketch_text.stroke-31")}),-1.0]])]});
            var Q3;
            Q3=makeQuery(id+"F24.imprint","IMPRINT",FACE,{"disambiguationData":[TD([[makeQuery(id+"F24.imprint","IMPRINT",EDGE,{"derivedFrom":sQuery(id+"F24.wireOp",EDGE,"E72.sketch_text.stroke-39")}),-1.0]])]});
            var Q4;
            Q4=makeQuery(id+"F24.imprint","IMPRINT",FACE,{"disambiguationData":[TD([[makeQuery(id+"F24.imprint","IMPRINT",EDGE,{"derivedFrom":sQuery(id+"F24.wireOp",EDGE,"E72.sketch_text.stroke-55")}),-1.0]])]});
            var Q5;
            Q5=makeQuery(id+"F24.imprint","IMPRINT",FACE,{"disambiguationData":[TD([[makeQuery(id+"F24.imprint","IMPRINT",EDGE,{"derivedFrom":sQuery(id+"F24.wireOp",EDGE,"E72.sketch_text.stroke-80")}),-1.0]])]});
            var Q6;
            Q6=makeQuery(id+"F24.imprint","IMPRINT",FACE,{"disambiguationData":[TD([[makeQuery(id+"F24.imprint","IMPRINT",EDGE,{"derivedFrom":sQuery(id+"F24.wireOp",EDGE,"E72.sketch_text.stroke-92")}),-1.0]])]});
            var Q7;
            Q7=makeQuery(id+"F24.imprint","IMPRINT",FACE,{"disambiguationData":[TD([[makeQuery(id+"F24.imprint","IMPRINT",EDGE,{"derivedFrom":sQuery(id+"F24.wireOp",EDGE,"E72.sketch_text.stroke-98")}),-1.0]])]});
            extrude(context, id + "F31", {"entities" : qUnion([Q0, Q1, Q2, Q3, Q4, Q5, Q6, Q7]), "operationType" : NewBodyOperationType.ADD, "depth" : 2 * mm});
        }
        {
            var Q0;
            Q0=makeQuery(id+"F22.imprint","IMPRINT",FACE,{"disambiguationData":[TD([[makeQuery(id+"F22.imprint","IMPRINT",EDGE,{"derivedFrom":sQuery(id+"F22.wireOp",EDGE,"E67.sketch_text.stroke-0")}),-1.0]])]});
            var Q1;
            Q1=makeQuery(id+"F22.imprint","IMPRINT",FACE,{"disambiguationData":[TD([[makeQuery(id+"F22.imprint","IMPRINT",EDGE,{"derivedFrom":sQuery(id+"F22.wireOp",EDGE,"E67.sketch_text.stroke-25")}),-1.0]])]});
            var Q2;
            Q2=makeQuery(id+"F22.imprint","IMPRINT",FACE,{"disambiguationData":[TD([[makeQuery(id+"F22.imprint","IMPRINT",EDGE,{"derivedFrom":sQuery(id+"F22.wireOp",EDGE,"E67.sketch_text.stroke-37")}),-1.0]])]});
            var Q3;
            Q3=makeQuery(id+"F22.imprint","IMPRINT",FACE,{"disambiguationData":[TD([[makeQuery(id+"F22.imprint","IMPRINT",EDGE,{"derivedFrom":sQuery(id+"F22.wireOp",EDGE,"E67.sketch_text.stroke-52")}),-1.0]])]});
            var Q4;
            Q4=makeQuery(id+"F22.imprint","IMPRINT",FACE,{"disambiguationData":[TD([[makeQuery(id+"F22.imprint","IMPRINT",EDGE,{"derivedFrom":sQuery(id+"F22.wireOp",EDGE,"E67.sketch_text.stroke-60")}),-1.0]])]});
            var Q5;
            Q5=makeQuery(id+"F22.imprint","IMPRINT",FACE,{"disambiguationData":[TD([[makeQuery(id+"F22.imprint","IMPRINT",EDGE,{"derivedFrom":sQuery(id+"F22.wireOp",EDGE,"E67.sketch_text.stroke-72")}),-1.0]])]});
            var Q6;
            Q6=makeQuery(id+"F22.imprint","IMPRINT",FACE,{"disambiguationData":[TD([[makeQuery(id+"F22.imprint","IMPRINT",EDGE,{"derivedFrom":sQuery(id+"F22.wireOp",EDGE,"E67.sketch_text.stroke-90")}),-1.0]])]});
            var Q7;
            Q7=makeQuery(id+"F22.imprint","IMPRINT",FACE,{"disambiguationData":[TD([[makeQuery(id+"F22.imprint","IMPRINT",EDGE,{"derivedFrom":sQuery(id+"F22.wireOp",EDGE,"E67.sketch_text.stroke-115")}),-1.0]])]});
            var Q8;
            Q8=makeQuery(id+"F22.imprint","IMPRINT",FACE,{"disambiguationData":[TD([[makeQuery(id+"F22.imprint","IMPRINT",EDGE,{"derivedFrom":sQuery(id+"F22.wireOp",EDGE,"E67.sketch_text.stroke-127")}),-1.0]])]});
            var Q9;
            Q9=makeQuery(id+"F22.imprint","IMPRINT",FACE,{"disambiguationData":[TD([[makeQuery(id+"F22.imprint","IMPRINT",EDGE,{"derivedFrom":sQuery(id+"F22.wireOp",EDGE,"E67.sketch_text.stroke-133")}),-1.0]])]});
            extrude(context, id + "F32", {"entities" : qUnion([Q0, Q1, Q2, Q3, Q4, Q5, Q6, Q7, Q8, Q9]), "operationType" : NewBodyOperationType.ADD, "depth" : 2 * mm});
        }
        {
            var Q0;
            Q0=makeQuery(id+"F20.imprint","IMPRINT",FACE,{"disambiguationData":[TD([[makeQuery(id+"F20.imprint","IMPRINT",EDGE,{"derivedFrom":sQuery(id+"F20.wireOp",EDGE,"E57.sketch_text.stroke-0")}),-1.0]])]});
            var Q1;
            Q1=makeQuery(id+"F20.imprint","IMPRINT",FACE,{"disambiguationData":[TD([[makeQuery(id+"F20.imprint","IMPRINT",EDGE,{"derivedFrom":sQuery(id+"F20.wireOp",EDGE,"E57.sketch_text.stroke-13")}),-1.0]])]});
            var Q2;
            Q2=makeQuery(id+"F20.imprint","IMPRINT",FACE,{"disambiguationData":[TD([[makeQuery(id+"F20.imprint","IMPRINT",EDGE,{"derivedFrom":sQuery(id+"F20.wireOp",EDGE,"E57.sketch_text.stroke-27")}),-1.0]])]});
            var Q3;
            Q3=makeQuery(id+"F20.imprint","IMPRINT",FACE,{"disambiguationData":[TD([[makeQuery(id+"F20.imprint","IMPRINT",EDGE,{"derivedFrom":sQuery(id+"F20.wireOp",EDGE,"E57.sketch_text.stroke-47")}),-1.0]])]});
            var Q4;
            Q4=makeQuery(id+"F20.imprint","IMPRINT",FACE,{"disambiguationData":[TD([[makeQuery(id+"F20.imprint","IMPRINT",EDGE,{"derivedFrom":sQuery(id+"F20.wireOp",EDGE,"E57.sketch_text.stroke-29")}),-1.0]])]});
            extrude(context, id + "F33", {"entities" : qUnion([Q0, Q1, Q2, Q3, Q4]), "operationType" : NewBodyOperationType.ADD, "depth" : 2 * mm});
        }
        {
            var Q0;
            Q0=makeQuery(id+"F18.imprint","IMPRINT",FACE,{"disambiguationData":[TD([[makeQuery(id+"F18.imprint","IMPRINT",EDGE,{"derivedFrom":sQuery(id+"F18.wireOp",EDGE,"E48.sketch_text.stroke-0")}),-1.0]])]});
            var Q1;
            Q1=makeQuery(id+"F18.imprint","IMPRINT",FACE,{"disambiguationData":[TD([[makeQuery(id+"F18.imprint","IMPRINT",EDGE,{"derivedFrom":sQuery(id+"F18.wireOp",EDGE,"E48.sketch_text.stroke-10")}),-1.0]])]});
            var Q2;
            Q2=makeQuery(id+"F18.imprint","IMPRINT",FACE,{"disambiguationData":[TD([[makeQuery(id+"F18.imprint","IMPRINT",EDGE,{"derivedFrom":sQuery(id+"F18.wireOp",EDGE,"E48.sketch_text.stroke-24")}),-1.0]])]});
            var Q3;
            Q3=makeQuery(id+"F18.imprint","IMPRINT",FACE,{"disambiguationData":[TD([[makeQuery(id+"F18.imprint","IMPRINT",EDGE,{"derivedFrom":sQuery(id+"F18.wireOp",EDGE,"E48.sketch_text.stroke-30")}),-1.0]])]});
            var Q4;
            Q4=makeQuery(id+"F18.imprint","IMPRINT",FACE,{"disambiguationData":[TD([[makeQuery(id+"F18.imprint","IMPRINT",EDGE,{"derivedFrom":sQuery(id+"F18.wireOp",EDGE,"E48.sketch_text.stroke-36")}),-1.0]])]});
            var Q5;
            Q5=makeQuery(id+"F18.imprint","IMPRINT",FACE,{"disambiguationData":[TD([[makeQuery(id+"F18.imprint","IMPRINT",EDGE,{"derivedFrom":sQuery(id+"F18.wireOp",EDGE,"E48.sketch_text.stroke-40")}),-1.0]])]});
            var Q6;
            Q6=makeQuery(id+"F18.imprint","IMPRINT",FACE,{"disambiguationData":[TD([[makeQuery(id+"F18.imprint","IMPRINT",EDGE,{"derivedFrom":sQuery(id+"F18.wireOp",EDGE,"E48.sketch_text.stroke-52")}),-1.0]])]});
            extrude(context, id + "F34", {"entities" : qUnion([Q0, Q1, Q2, Q3, Q4, Q5, Q6]), "operationType" : NewBodyOperationType.ADD, "depth" : 2 * mm});
        }
        {
            var Q0;
            Q0=makeQuery(id+"F16.imprint","IMPRINT",FACE,{"disambiguationData":[TD([[makeQuery(id+"F16.imprint","IMPRINT",EDGE,{"derivedFrom":sQuery(id+"F16.wireOp",EDGE,"E40.sketch_text.stroke-0")}),-1.0]])]});
            var Q1;
            Q1=makeQuery(id+"F16.imprint","IMPRINT",FACE,{"disambiguationData":[TD([[makeQuery(id+"F16.imprint","IMPRINT",EDGE,{"derivedFrom":sQuery(id+"F16.wireOp",EDGE,"E40.sketch_text.stroke-10")}),-1.0]])]});
            var Q2;
            Q2=makeQuery(id+"F16.imprint","IMPRINT",FACE,{"disambiguationData":[TD([[makeQuery(id+"F16.imprint","IMPRINT",EDGE,{"derivedFrom":sQuery(id+"F16.wireOp",EDGE,"E40.sketch_text.stroke-24")}),-1.0]])]});
            var Q3;
            Q3=makeQuery(id+"F16.imprint","IMPRINT",FACE,{"disambiguationData":[TD([[makeQuery(id+"F16.imprint","IMPRINT",EDGE,{"derivedFrom":sQuery(id+"F16.wireOp",EDGE,"E40.sketch_text.stroke-39")}),-1.0]])]});
            extrude(context, id + "F35", {"entities" : qUnion([Q0, Q1, Q2, Q3]), "operationType" : NewBodyOperationType.ADD, "depth" : 2 * mm});
        }
        {
            var Q0;
            Q0=makeQuery(id+"F14.imprint","IMPRINT",FACE,{"disambiguationData":[TD([[makeQuery(id+"F14.imprint","IMPRINT",EDGE,{"derivedFrom":sQuery(id+"F14.wireOp",EDGE,"E33.sketch_text.stroke-0")}),-1.0]])]});
            var Q1;
            Q1=makeQuery(id+"F14.imprint","IMPRINT",FACE,{"disambiguationData":[TD([[makeQuery(id+"F14.imprint","IMPRINT",EDGE,{"derivedFrom":sQuery(id+"F14.wireOp",EDGE,"E33.sketch_text.stroke-18")}),-1.0]])]});
            var Q2;
            Q2=makeQuery(id+"F14.imprint","IMPRINT",FACE,{"disambiguationData":[TD([[makeQuery(id+"F14.imprint","IMPRINT",EDGE,{"derivedFrom":sQuery(id+"F14.wireOp",EDGE,"E33.sketch_text.stroke-31")}),-1.0]])]});
            extrude(context, id + "F36", {"entities" : qUnion([Q0, Q1, Q2]), "operationType" : NewBodyOperationType.ADD, "depth" : 2 * mm});
        }
        {
            var Q0;
            Q0=makeQuery(id+"F0.imprint","IMPRINT",FACE,{"disambiguationData":[TD([[makeQuery(id+"F0.imprint","IMPRINT",EDGE,{"derivedFrom":sQuery(id+"F0.wireOp",EDGE,"E0.bottom")}),-1.0]])]});
            extrude(context, id + "F37", {"entities" : qUnion([Q0]), "depth" : 3 * mm});
        }
    });
